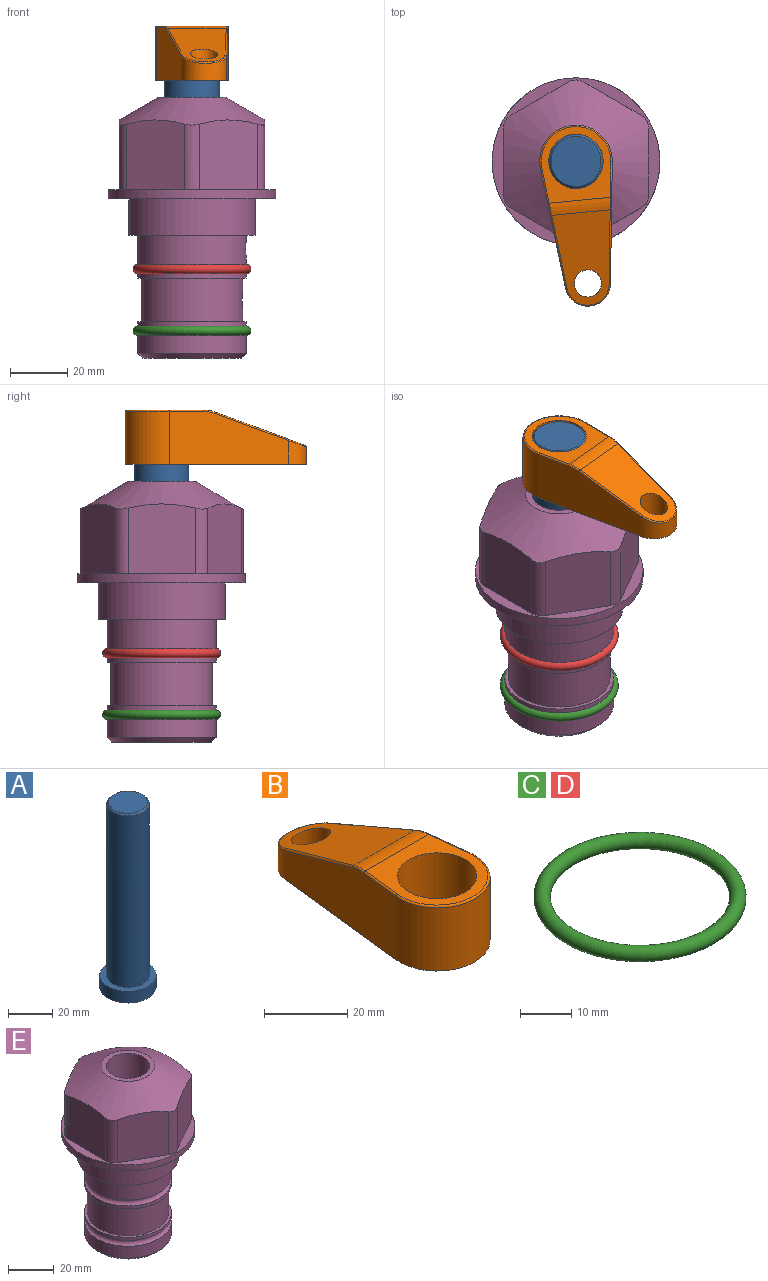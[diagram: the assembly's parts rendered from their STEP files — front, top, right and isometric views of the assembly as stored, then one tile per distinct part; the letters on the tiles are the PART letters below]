
ASSEMBLY  parts=5 mates=3
PART A: 6 faces, bbox 25.4x25.4x101.6 mm
  f0: plane 17.46x17.46mm, normal (0,0,1), area 239.5mm2, adj f5
  f1: plane 25.4x25.4mm, normal (0,0,-1), area 506.7mm2, adj f2
  f2: cylinder r=12.7mm len=25.4mm, axis (0,0,1), area 506.7mm2, adj f1,f3
  f3: plane 25.4x25.4mm, normal (0,0,1), area 221.7mm2, adj f2,f4
  f4: cylinder r=9.53mm len=94.46mm, axis (0,0,1), area 5653mm2, adj f3,f5
  f5: cone r=8.73mm half-angle=45deg, axis (0,0,-1), area 64.4mm2, adj f0,f4
PART B: 44 faces, bbox 27.5x64.5x19.1 mm
  f0: plane 2.3x0.95mm, normal (0,0,-1), area 1mm2, adj f25,f30,f34
  f1: plane 63.5x25.4mm, normal (0,0,-1), area 561.7mm2, adj f2,f3,f4,f5,f6,f7,f19,f20
  f2: cylinder r=12.7mm len=25.4mm, axis (0,0,-1), area 792.2mm2, adj f1,f3,f5,f13
  f3: plane 42.33x18.54mm, normal (0.99,0.11,0), area 647mm2, adj f1,f2,f4,f11,f12,f14
  f4: cylinder r=7.94mm len=15.78mm, axis (0,0,-1), area 158.6mm2, adj f1,f3,f5,f16
  f5: plane 42.33x18.54mm, normal (-0.99,0.11,0), area 647mm2, adj f1,f2,f4,f15,f17,f18
  f6: cylinder r=9.53mm len=19.05mm, axis (0,0,-1), area 1140.1mm2, adj f1,f8
  f7: cylinder r=4.76mm len=10.98mm, axis (0,0,-1), area 276.1mm2, adj f1,f9
  f8: plane 25.83x24.38mm, normal (0,0,1), area 262.2mm2, adj f6,f10,f11,f13,f15
  f9: plane 32.49x20.55mm, normal (0,0.34,0.94), area 489.9mm2, adj f7,f10,f14,f16,f18
  f10: cylinder r=12.7mm len=21.49mm, axis (-1,0,0), area 93.2mm2, adj f8,f9,f12,f17
  f11: cylinder r=0.51mm len=12.34mm, axis (0.11,-0.99,0), area 9.9mm2, adj f3,f8,f12,f13
  f12: bspline ~7.62x1.64mm, area 3.5mm2, adj f3,f10,f11,f14
  f13: torus R=12.19mm, axis (0,0,1), area 33.6mm2, adj f2,f8,f11,f15
  f14: cylinder r=0.51mm len=26.01mm, axis (0.1,-0.93,0.34), area 21.6mm2, adj f3,f9,f12,f16
  f15: cylinder r=0.51mm len=12.34mm, axis (0.11,0.99,0), area 9.9mm2, adj f5,f8,f13,f17
  f16: bspline ~15.78x7.05mm, area 15.7mm2, adj f4,f9,f14,f18
  f17: bspline ~7.62x1.64mm, area 3.5mm2, adj f5,f10,f15,f18
  f18: cylinder r=0.51mm len=26.01mm, axis (0.1,0.93,-0.34), area 21.6mm2, adj f5,f9,f16,f17
  f19: plane 21.6x14.29mm, normal (-0.99,-0.11,0), area 242.6mm2, adj f1,f26,f28,f34,f36,f38
  f20: plane 21.6x14.29mm, normal (0.99,-0.11,0), area 242.6mm2, adj f1,f27,f29,f37,f39,f41
  f21: cylinder r=12.7mm len=14.29mm, axis (0,0,-1), area 173.2mm2, adj f1,f26,f27,f30,f31,f33
  f22: cylinder r=7.94mm len=7.63mm, axis (0,0,-1), area 53.8mm2, adj f1,f28,f29,f42
  f23: plane 2.3x0.95mm, normal (0,0,-1), area 1mm2, adj f25,f33,f37
  f24: plane 17.94x12.32mm, normal (0,-0.34,-0.94), area 191.2mm2, adj f25,f38,f41,f42
  f25: cylinder r=9.53mm len=12.93mm, axis (-1,0,0), area 37.5mm2, adj f0,f23,f24,f31,f36,f39
  f26: cylinder r=1.59mm len=14.29mm, axis (0,0,-1), area 49mm2, adj f1,f19,f21,f32
  f27: cylinder r=1.59mm len=14.29mm, axis (0,0,-1), area 49mm2, adj f1,f20,f21,f35
  f28: cylinder r=1.59mm len=7.28mm, axis (0,0,-1), area 22.1mm2, adj f1,f19,f22,f40
  f29: cylinder r=1.59mm len=7.28mm, axis (0,0,-1), area 22.1mm2, adj f1,f20,f22,f43
  f30: torus R=14.29mm, axis (0,0,1), area 5.8mm2, adj f0,f21,f31,f32
  f31: bspline ~11.06x2.73mm, area 20.8mm2, adj f21,f25,f30,f33
  f32: sphere r=1.59mm, area 5.4mm2, adj f26,f30,f34
  f33: torus R=14.29mm, axis (0,0,1), area 5.8mm2, adj f21,f23,f31,f35
  f34: cylinder r=1.59mm len=1.68mm, axis (-0.11,0.99,0), area 2.4mm2, adj f0,f19,f32,f36
  f35: sphere r=1.59mm, area 5.4mm2, adj f27,f33,f37
  f36: bspline ~5.82x2.33mm, area 7.7mm2, adj f19,f25,f34,f38
  f37: cylinder r=1.59mm len=1.68mm, axis (0.11,0.99,0), area 2.4mm2, adj f20,f23,f35,f39
  f38: cylinder r=1.59mm len=18.33mm, axis (0.1,-0.93,0.34), area 46.7mm2, adj f19,f24,f36,f40
  f39: bspline ~5.82x2.33mm, area 7.7mm2, adj f20,f25,f37,f41
  f40: sphere r=1.59mm, area 3.6mm2, adj f28,f38,f42
  f41: cylinder r=1.59mm len=18.33mm, axis (0.1,0.93,-0.34), area 46.7mm2, adj f20,f24,f39,f43
  f42: bspline ~8.31x1.84mm, area 15.3mm2, adj f22,f24,f40,f43
  f43: sphere r=1.59mm, area 3.6mm2, adj f29,f41,f42
PART C: 1 faces, bbox 44.7x44.7x3.2 mm
  f0: torus R=19.05mm, axis (0,0,1), area 1193.9mm2
PART D: same geometry as C
PART E: 36 faces, bbox 58.7x58.7x91.2 mm
  f0: cylinder r=17.78mm len=35.56mm, axis (0,0,1), area 1670.8mm2, adj f23,f24,f31
  f1: cylinder r=19.05mm len=38.1mm, axis (0,0,1), area 1191.9mm2, adj f26,f27,f30
  f2: plane 58.66x58.66mm, normal (0,0,-1), area 1150.6mm2, adj f3,f28
  f3: cylinder r=29.33mm len=58.66mm, axis (0,0,-1), area 585.1mm2, adj f2,f4
  f4: plane 58.66x58.66mm, normal (0,0,1), area 475.9mm2, adj f3,f5,f6,f7,f8,f9,f10,f11
  f5: plane 24.5x20.32mm, normal (-0.5,0.87,0), area 562.8mm2, adj f4,f15,f16,f17
  f6: plane 24.5x20.32mm, normal (0.5,0.87,0), area 562.8mm2, adj f4,f14,f15,f17
  f7: plane 24.5x23.48mm, normal (1,0,0), area 562.8mm2, adj f4,f13,f14,f17
  f8: plane 24.5x20.32mm, normal (0.5,-0.87,0), area 562.8mm2, adj f4,f12,f13,f17
  f9: plane 24.5x20.32mm, normal (-0.5,-0.87,0), area 562.8mm2, adj f4,f11,f12,f17
  f10: plane 24.5x23.48mm, normal (-1,0,0), area 562.8mm2, adj f4,f11,f16,f17
  f11: cylinder r=5.08mm len=23.01mm, axis (0,0,-1), area 121.2mm2, adj f4,f9,f10,f17
  f12: cylinder r=5.08mm len=23.01mm, axis (0,0,-1), area 121.2mm2, adj f4,f8,f9,f17
  f13: cylinder r=5.08mm len=23.01mm, axis (0,0,-1), area 121.2mm2, adj f4,f7,f8,f17
  f14: cylinder r=5.08mm len=23.01mm, axis (0,0,-1), area 121.2mm2, adj f4,f6,f7,f17
  f15: cylinder r=5.08mm len=23.01mm, axis (0,0,-1), area 121.2mm2, adj f4,f5,f6,f17
  f16: cylinder r=5.08mm len=23.01mm, axis (0,0,-1), area 121.2mm2, adj f4,f5,f10,f17
  f17: cone r=11.73mm half-angle=60deg, axis (0,0,-1), area 2071.8mm2, adj f5,f6,f7,f8,f9,f10,f11,f12
  f18: plane 23.46x23.46mm, normal (0,0,1), area 147.4mm2, adj f17,f35
  f19: plane 34.93x34.93mm, normal (0,0,-1), area 958mm2, adj f29
  f20: cylinder r=19.05mm len=38.1mm, axis (0,0,1), area 760.1mm2, adj f21,f29
  f21: torus R=19.05mm, axis (0,0,1), area 565.3mm2, adj f20,f22
  f22: cylinder r=19.05mm len=38.1mm, axis (0,0,1), area 190mm2, adj f21,f23
  f23: plane 38.1x38.1mm, normal (0,0,1), area 146.9mm2, adj f0,f22
  f24: plane 38.1x38.1mm, normal (0,0,-1), area 146.9mm2, adj f0,f25
  f25: cylinder r=19.05mm len=38.1mm, axis (0,0,1), area 190mm2, adj f24,f26
  f26: torus R=19.05mm, axis (0,0,1), area 565.3mm2, adj f1,f25
  f27: plane 44.45x44.45mm, normal (0,0,-1), area 411.7mm2, adj f1,f28
  f28: cylinder r=22.23mm len=44.45mm, axis (0,0,1), area 1773.5mm2, adj f2,f27
  f29: cone r=19.05mm half-angle=45deg, axis (0,0,1), area 257.5mm2, adj f19,f20
  f30: cylinder r=3.17mm len=6.75mm, axis (-1,0,0), area 128mm2, adj f1,f33
  f31: cylinder r=3.17mm len=6.35mm, axis (-1,0,0), area 102.5mm2, adj f0,f33
  f32: plane 25.4x25.4mm, normal (0,0,1), area 506.7mm2, adj f33
  f33: cylinder r=12.7mm len=66.42mm, axis (0,0,-1), area 5236.2mm2, adj f30,f31,f32,f34
  f34: cone r=9.53mm half-angle=30deg, axis (0,0,-1), area 443.4mm2, adj f33,f35
  f35: cylinder r=9.53mm len=19.05mm, axis (0,0,-1), area 849mm2, adj f18,f34
PLACE A rot(axis=(0,0,-1),84.5deg) t=(0,0,-13.14)mm
PLACE B rot(axis=(0,0,-1),174.5deg) t=(0,0,41.47)mm
PLACE C t=(0,0,-21.59)mm
PLACE D at identity
PLACE E at identity fixed
MATE fastened C.f0 <-> E.f0  axis (0,0,1) through (0,0,-46.1)mm
MATE cylindrical A.f2 <-> E.f0  axis (0,0,1) through (0,0,12.5)mm
MATE fastened B.f2 <-> A.f2  axis (0,0,1) through (0,0,60.52)mm
